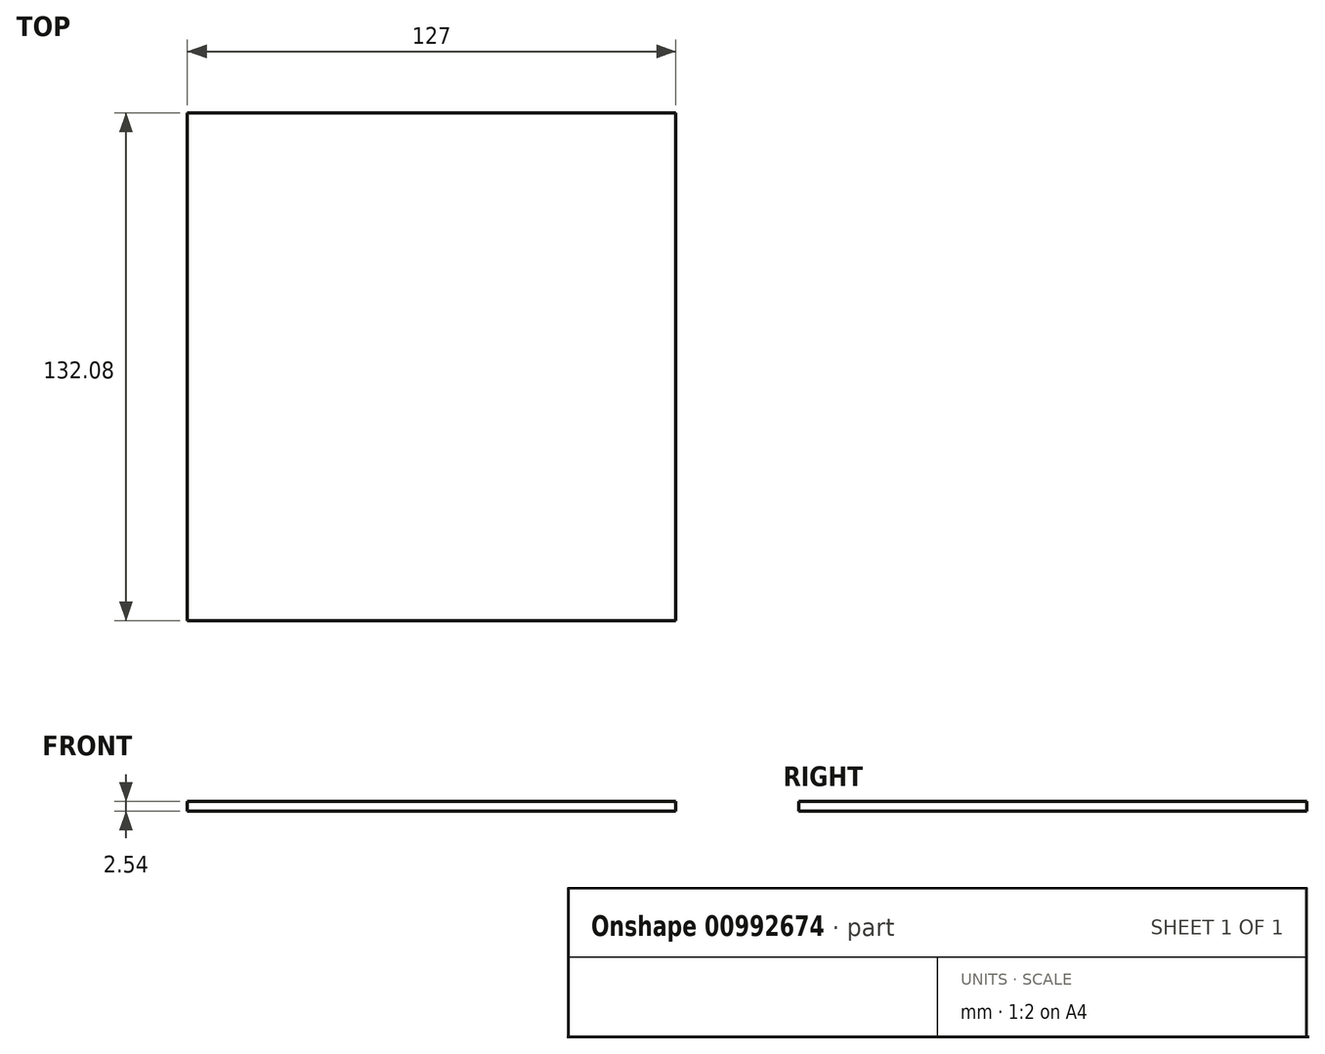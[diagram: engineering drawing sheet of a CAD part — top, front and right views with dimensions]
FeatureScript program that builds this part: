
annotation { "Feature Type Name" : "Feature", "Feature Type Description" : "" }
export const myFeature = defineFeature(function(context is Context, id is Id, definition is map)
    precondition{}
    {
        {
            var Q0;
            Q0=qCreatedBy(makeId("Top.planeOp"),FACE);
            var sketch = newSketch(context, id + "F0", { "sketchPlane" : qUnion([Q0])});
            skLineSegment(sketch, "E0.bottom", {"start": v(-88.71, 65.48) * mm, "end": v(38.29, 65.48) * mm});
            skLineSegment(sketch, "E0.top", {"start": v(-88.71, -66.6) * mm, "end": v(38.29, -66.6) * mm});
            skLineSegment(sketch, "E0.left", {"start": v(-88.71, 65.48) * mm, "end": v(-88.71, -66.6) * mm});
            skLineSegment(sketch, "E0.right", {"start": v(38.29, 65.48) * mm, "end": v(38.29, -66.6) * mm});
            skSolve(sketch);
        }
        {
            var Q0;
            Q0=makeQuery(id+"F0.imprint","IMPRINT",FACE,{"disambiguationData":[TD([[makeQuery(id+"F0.imprint","IMPRINT",EDGE,{"derivedFrom":sQuery(id+"F0.wireOp",EDGE,"E0.bottom")}),-1.0]])]});
            extrude(context, id + "F1", {"entities" : qUnion([Q0]), "depth" : 2.54 * mm, "offsetDistance" : 25.4 * mm});
        }
    });
